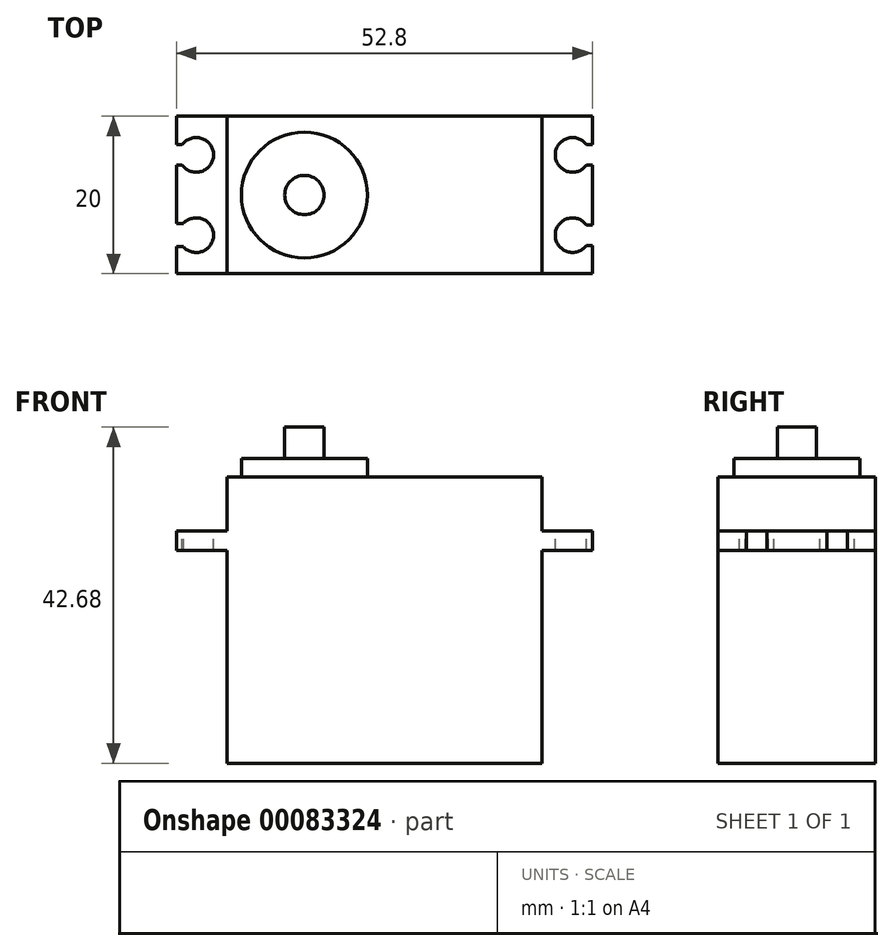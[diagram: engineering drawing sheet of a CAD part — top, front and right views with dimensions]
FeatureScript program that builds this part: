
annotation { "Feature Type Name" : "Feature", "Feature Type Description" : "" }
export const myFeature = defineFeature(function(context is Context, id is Id, definition is map)
    precondition{}
    {
        {
            var Q0;
            Q0=qCreatedBy(makeId("Top.planeOp"),FACE);
            var sketch = newSketch(context, id + "F0", { "sketchPlane" : qUnion([Q0])});
            skLineSegment(sketch, "E0.bottom", {"start": v(26.4, 10) * mm, "end": v(-26.4, 10) * mm});
            skLineSegment(sketch, "E0.top", {"start": v(26.4, -10) * mm, "end": v(-26.4, -10) * mm});
            skLineSegment(sketch, "E0.left", {"start": v(26.4, 10) * mm, "end": v(26.4, -10) * mm});
            skLineSegment(sketch, "E0.right", {"start": v(-26.4, 10) * mm, "end": v(-26.4, -10) * mm});
            skPoint(sketch, "E0.middle", {"position": v(0, 0) * mm});
            skSolve(sketch);
        }
        {
            var Q0;
            Q0 = qSketchRegion(id + "F0", true);
            extrude(context, id + "F1", {"entities" : qUnion([Q0]), "depth" : 2.5 * mm});
        }
        {
            var Q0;
            Q0=makeQuery(id+"F1.opExtrude","CAP_FACE",FACE,{"disambiguationData":[OSD([sQuery(id+"F0.wireOp",EDGE,"E0.bottom"),sQuery(id+"F0.wireOp",EDGE,"E0.top"),sQuery(id+"F0.wireOp",EDGE,"E0.left"),sQuery(id+"F0.wireOp",EDGE,"E0.right")])],"isStart":false});
            var sketch = newSketch(context, id + "F2", { "sketchPlane" : qUnion([Q0])});
            skLineSegment(sketch, "E1.bottom", {"start": v(-20, 10) * mm, "end": v(20, 10) * mm});
            skLineSegment(sketch, "E1.top", {"start": v(-20, -10) * mm, "end": v(20, -10) * mm});
            skLineSegment(sketch, "E1.left", {"start": v(-20, 10) * mm, "end": v(-20, -10) * mm});
            skLineSegment(sketch, "E1.right", {"start": v(20, 10) * mm, "end": v(20, -10) * mm});
            skSolve(sketch);
        }
        {
            var Q0;
            Q0 = qSketchRegion(id + "F2", true);
            extrude(context, id + "F3", {"entities" : qUnion([Q0]), "operationType" : NewBodyOperationType.ADD, "depth" : 6.85 * mm});
        }
        {
            var Q0;
            Q0=makeQuery(id+"F1.opExtrude","CAP_FACE",FACE,{"disambiguationData":[OSD([sQuery(id+"F0.wireOp",EDGE,"E0.bottom"),sQuery(id+"F0.wireOp",EDGE,"E0.top"),sQuery(id+"F0.wireOp",EDGE,"E0.left"),sQuery(id+"F0.wireOp",EDGE,"E0.right")])],"isStart":true});
            var sketch = newSketch(context, id + "F4", { "sketchPlane" : qUnion([Q0])});
            skLineSegment(sketch, "E2.bottom", {"start": v(-20, 10) * mm, "end": v(20, 10) * mm});
            skLineSegment(sketch, "E2.top", {"start": v(-20, -10) * mm, "end": v(20, -10) * mm});
            skLineSegment(sketch, "E2.left", {"start": v(-20, 10) * mm, "end": v(-20, -10) * mm});
            skLineSegment(sketch, "E2.right", {"start": v(20, 10) * mm, "end": v(20, -10) * mm});
            skSolve(sketch);
        }
        {
            var Q0;
            Q0 = qSketchRegion(id + "F4", true);
            extrude(context, id + "F5", {"entities" : qUnion([Q0]), "operationType" : NewBodyOperationType.ADD, "depth" : 27 * mm});
        }
        {
            var Q0;
            {var subQ0=sQuery(id+"F0.wireOp",EDGE,"E0.left");var subQ1=sQuery(id+"F0.wireOp",EDGE,"E0.top");var subQ2=sQuery(id+"F0.wireOp",EDGE,"E0.bottom");Q0=makeQuery(id+"F3.boolean.opBoolean","SPLIT",FACE,{"disambiguationData":[TD([makeQuery(id+"F1.opExtrude","SWEPT_FACE",FACE,{"disambiguationData":[OSD([subQ0])]})])],"derivedFrom":makeQuery(id+"F1.opExtrude","CAP_FACE",FACE,{"disambiguationData":[OSD([subQ2,subQ1,subQ0,sQuery(id+"F0.wireOp",EDGE,"E0.right")])],"isStart":false})});}
            var sketch = newSketch(context, id + "F6", { "sketchPlane" : qUnion([Q0])});
            skCircle(sketch, "E3", {"center": v(-23.9, 5.1) * mm, "radius": 2.2 * mm});
            skCircle(sketch, "E4", {"center": v(-23.9, -5.1) * mm, "radius": 2.2 * mm});
            skCircle(sketch, "E5", {"center": v(23.9, 5.1) * mm, "radius": 2.2 * mm});
            skCircle(sketch, "E6", {"center": v(23.9, -5.1) * mm, "radius": 2.2 * mm});
            skLineSegment(sketch, "E7", {"start": v(-31.26, 0) * mm, "end": v(26.4, 0) * mm, "construction": true});
            skLineSegment(sketch, "E8", {"start": v(0, 20.3) * mm, "end": v(0, -21.65) * mm, "construction": true});
            skSolve(sketch);
        }
        {
            var Q0;
            Q0 = qSketchRegion(id + "F6", true);
            extrude(context, id + "F7", {"entities" : qUnion([Q0]), "operationType" : NewBodyOperationType.REMOVE, "endBound" : BoundingType.UP_TO_NEXT, "oppositeDirection" : true, "depth" : 25 * mm});
        }
        {
            var Q0;
            {var subQ0=sQuery(id+"F0.wireOp",EDGE,"E0.right");var subQ1=sQuery(id+"F0.wireOp",EDGE,"E0.top");var subQ2=sQuery(id+"F0.wireOp",EDGE,"E0.bottom");Q0=makeQuery(id+"F3.boolean.opBoolean","SPLIT",FACE,{"disambiguationData":[TD([makeQuery(id+"F1.opExtrude","SWEPT_FACE",FACE,{"disambiguationData":[OSD([subQ0])]})])],"derivedFrom":makeQuery(id+"F1.opExtrude","CAP_FACE",FACE,{"disambiguationData":[OSD([subQ2,subQ1,sQuery(id+"F0.wireOp",EDGE,"E0.left"),subQ0])],"isStart":false})});}
            var sketch = newSketch(context, id + "F8", { "sketchPlane" : qUnion([Q0])});
            skLineSegment(sketch, "E9.bottom", {"start": v(-26.4, 6.4) * mm, "end": v(-25.67, 6.4) * mm});
            skLineSegment(sketch, "E9.top", {"start": v(-26.4, 3.8) * mm, "end": v(-25.67, 3.8) * mm});
            skLineSegment(sketch, "E9.left", {"start": v(-26.4, 6.4) * mm, "end": v(-26.4, 3.8) * mm});
            skLineSegment(sketch, "E9.right", {"start": v(-25.67, 6.4) * mm, "end": v(-25.67, 3.8) * mm});
            skLineSegment(sketch, "E10.bottom", {"start": v(-26.4, -3.64) * mm, "end": v(-25.54, -3.64) * mm});
            skLineSegment(sketch, "E10.top", {"start": v(-26.4, -6.56) * mm, "end": v(-25.54, -6.56) * mm});
            skLineSegment(sketch, "E10.left", {"start": v(-26.4, -3.64) * mm, "end": v(-26.4, -6.56) * mm});
            skLineSegment(sketch, "E10.right", {"start": v(-25.54, -3.64) * mm, "end": v(-25.54, -6.56) * mm});
            skSolve(sketch);
        }
        {
            var Q0;
            Q0 = qSketchRegion(id + "F8", true);
            extrude(context, id + "F9", {"entities" : qUnion([Q0]), "operationType" : NewBodyOperationType.REMOVE, "oppositeDirection" : true, "depth" : 4 * mm});
        }
        {
            var Q0;
            {var subQ0=sQuery(id+"F0.wireOp",EDGE,"E0.left");var subQ1=sQuery(id+"F0.wireOp",EDGE,"E0.top");var subQ2=sQuery(id+"F0.wireOp",EDGE,"E0.bottom");Q0=makeQuery(id+"F3.boolean.opBoolean","SPLIT",FACE,{"disambiguationData":[TD([makeQuery(id+"F1.opExtrude","SWEPT_FACE",FACE,{"disambiguationData":[OSD([subQ0])]})])],"derivedFrom":makeQuery(id+"F1.opExtrude","CAP_FACE",FACE,{"disambiguationData":[OSD([subQ2,subQ1,subQ0,sQuery(id+"F0.wireOp",EDGE,"E0.right")])],"isStart":false})});}
            var sketch = newSketch(context, id + "F10", { "sketchPlane" : qUnion([Q0])});
            skLineSegment(sketch, "E11.bottom", {"start": v(25.67, 6.4) * mm, "end": v(26.4, 6.4) * mm});
            skLineSegment(sketch, "E11.top", {"start": v(25.67, 3.8) * mm, "end": v(26.4, 3.8) * mm});
            skLineSegment(sketch, "E11.left", {"start": v(25.67, 6.4) * mm, "end": v(25.67, 3.8) * mm});
            skLineSegment(sketch, "E11.right", {"start": v(26.4, 6.4) * mm, "end": v(26.4, 3.8) * mm});
            skLineSegment(sketch, "E12.bottom", {"start": v(25.67, -3.8) * mm, "end": v(26.4, -3.8) * mm});
            skLineSegment(sketch, "E12.top", {"start": v(25.67, -6.4) * mm, "end": v(26.4, -6.4) * mm});
            skLineSegment(sketch, "E12.left", {"start": v(25.67, -3.8) * mm, "end": v(25.67, -6.4) * mm});
            skLineSegment(sketch, "E12.right", {"start": v(26.4, -3.8) * mm, "end": v(26.4, -6.4) * mm});
            skSolve(sketch);
        }
        {
            var Q0;
            Q0 = qSketchRegion(id + "F10", true);
            extrude(context, id + "F11", {"entities" : qUnion([Q0]), "operationType" : NewBodyOperationType.REMOVE, "oppositeDirection" : true, "depth" : 5 * mm});
        }
        {
            var Q0;
            Q0=makeQuery(id+"F3.opExtrude","CAP_FACE",FACE,{"disambiguationData":[OSD([sQuery(id+"F2.wireOp",EDGE,"E1.bottom"),sQuery(id+"F2.wireOp",EDGE,"E1.top"),sQuery(id+"F2.wireOp",EDGE,"E1.left"),sQuery(id+"F2.wireOp",EDGE,"E1.right")])],"isStart":false});
            var sketch = newSketch(context, id + "F12", { "sketchPlane" : qUnion([Q0])});
            skCircle(sketch, "E13", {"center": v(-10.16, 0) * mm, "radius": 8 * mm});
            skSolve(sketch);
        }
        {
            var Q0;
            Q0 = qSketchRegion(id + "F12", true);
            extrude(context, id + "F13", {"entities" : qUnion([Q0]), "operationType" : NewBodyOperationType.ADD, "depth" : 2.33 * mm});
        }
        {
            var Q0;
            Q0=makeQuery(id+"F13.opExtrude","CAP_FACE",FACE,{"disambiguationData":[OSD([sQuery(id+"F12.wireOp",EDGE,"E13")])],"isStart":false});
            var sketch = newSketch(context, id + "F14", { "sketchPlane" : qUnion([Q0])});
            skCircle(sketch, "E14", {"center": v(-10.16, 0) * mm, "radius": 2.5 * mm});
            skSolve(sketch);
        }
        {
            var Q0;
            Q0 = qSketchRegion(id + "F14", true);
            extrude(context, id + "F15", {"entities" : qUnion([Q0]), "operationType" : NewBodyOperationType.ADD, "depth" : 4 * mm});
        }
    });
